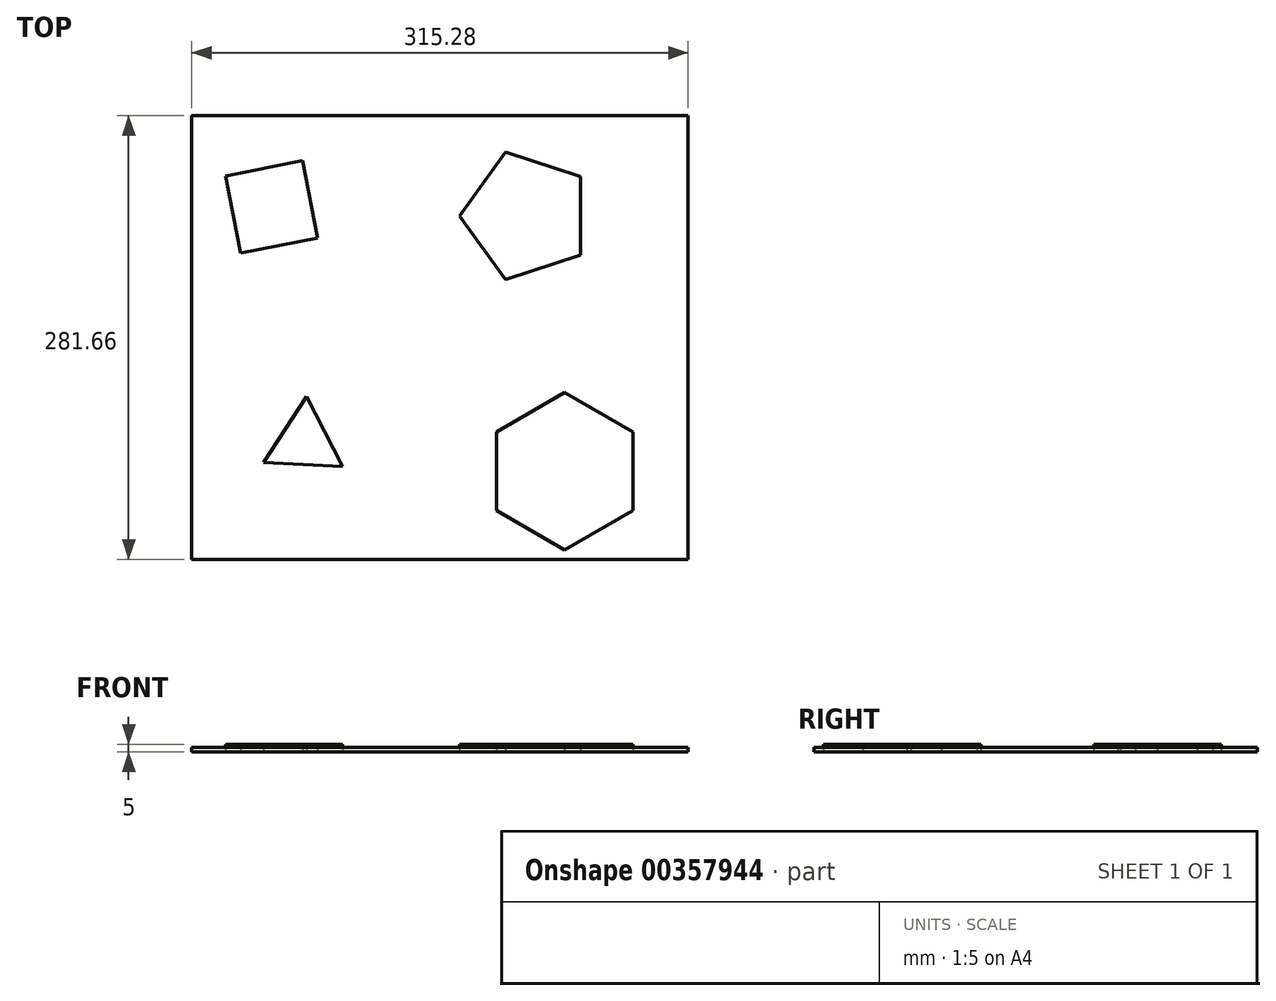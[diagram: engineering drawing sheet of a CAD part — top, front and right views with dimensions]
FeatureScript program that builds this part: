
annotation { "Feature Type Name" : "Feature", "Feature Type Description" : "" }
export const myFeature = defineFeature(function(context is Context, id is Id, definition is map)
    precondition{}
    {
        {
            var Q0;
            Q0=qCreatedBy(makeId("Top.planeOp"),FACE);
            var sketch = newSketch(context, id + "F0", { "sketchPlane" : qUnion([Q0])});
            skLineSegment(sketch, "E0.bottom", {"start": v(157.64, 140.83) * mm, "end": v(-157.64, 140.83) * mm});
            skLineSegment(sketch, "E0.top", {"start": v(157.64, -140.83) * mm, "end": v(-157.64, -140.83) * mm});
            skLineSegment(sketch, "E0.left", {"start": v(157.64, 140.83) * mm, "end": v(157.64, -140.83) * mm});
            skLineSegment(sketch, "E0.right", {"start": v(-157.64, 140.83) * mm, "end": v(-157.64, -140.83) * mm});
            skPoint(sketch, "E0.middle", {"position": v(0, 0) * mm});
            skSolve(sketch);
        }
        {
            var Q0;
            Q0=makeQuery(id+"F0.imprint","IMPRINT",FACE,{"disambiguationData":[TD([[makeQuery(id+"F0.imprint","IMPRINT",EDGE,{"derivedFrom":sQuery(id+"F0.wireOp",EDGE,"E0.bottom")}),1.0]])]});
            extrude(context, id + "F1", {"entities" : qUnion([Q0]), "depth" : 3 * mm});
        }
        {
            var Q0;
            Q0=qCreatedBy(makeId("Top.planeOp"),FACE);
            var sketch = newSketch(context, id + "F2", { "sketchPlane" : qUnion([Q0])});
            skCircle(sketch, "E1.cCircle", {"center": v(-86.17, -66.22) * mm, "radius": 14.43 * mm, "construction": true});
            skLineSegment(sketch, "E1.0", {"start": v(-84.62, -37.4) * mm, "end": v(-61.98, -81.97) * mm});
            skLineSegment(sketch, "E1.1", {"start": v(-61.98, -81.97) * mm, "end": v(-111.9, -79.3) * mm});
            skLineSegment(sketch, "E1.2", {"start": v(-111.9, -79.3) * mm, "end": v(-84.62, -37.4) * mm});
            skPoint(sketch, "E1.0.midPoint", {"position": v(-73.3, -59.68) * mm});
            skCircle(sketch, "E2.cCircle", {"center": v(-106.97, 82.94) * mm, "radius": 25 * mm, "construction": true});
            skLineSegment(sketch, "E2.0", {"start": v(-87.26, 112.3) * mm, "end": v(-77.61, 63.23) * mm});
            skLineSegment(sketch, "E2.1", {"start": v(-77.61, 63.23) * mm, "end": v(-126.67, 53.58) * mm});
            skLineSegment(sketch, "E2.2", {"start": v(-126.67, 53.58) * mm, "end": v(-136.32, 102.64) * mm});
            skLineSegment(sketch, "E2.3", {"start": v(-136.32, 102.64) * mm, "end": v(-87.26, 112.3) * mm});
            skPoint(sketch, "E2.0.midPoint", {"position": v(-82.44, 87.76) * mm});
            skCircle(sketch, "E3.cCircle", {"center": v(54.84, 77.23) * mm, "radius": 34.4 * mm, "construction": true});
            skLineSegment(sketch, "E3.0", {"start": v(89.25, 102.23) * mm, "end": v(89.25, 52.23) * mm});
            skLineSegment(sketch, "E3.1", {"start": v(89.25, 52.23) * mm, "end": v(41.7, 36.78) * mm});
            skLineSegment(sketch, "E3.2", {"start": v(41.7, 36.78) * mm, "end": v(12.3, 77.23) * mm});
            skLineSegment(sketch, "E3.3", {"start": v(12.3, 77.23) * mm, "end": v(41.7, 117.68) * mm});
            skLineSegment(sketch, "E3.4", {"start": v(41.7, 117.68) * mm, "end": v(89.25, 102.23) * mm});
            skPoint(sketch, "E3.0.midPoint", {"position": v(89.25, 77.23) * mm});
            skCircle(sketch, "E4.cCircle", {"center": v(79.22, -85) * mm, "radius": 43.3 * mm, "construction": true});
            skLineSegment(sketch, "E4.0", {"start": v(122.52, -60) * mm, "end": v(122.52, -110) * mm});
            skLineSegment(sketch, "E4.1", {"start": v(122.52, -110) * mm, "end": v(79.22, -135) * mm});
            skLineSegment(sketch, "E4.2", {"start": v(79.22, -135) * mm, "end": v(35.92, -110) * mm});
            skLineSegment(sketch, "E4.3", {"start": v(35.92, -110) * mm, "end": v(35.92, -60) * mm});
            skLineSegment(sketch, "E4.4", {"start": v(35.92, -60) * mm, "end": v(79.22, -35) * mm});
            skLineSegment(sketch, "E4.5", {"start": v(79.22, -35) * mm, "end": v(122.52, -60) * mm});
            skPoint(sketch, "E4.0.midPoint", {"position": v(122.52, -85) * mm});
            skSolve(sketch);
        }
        {
            assignVariable(context, id + "F3", {"name" : "tile_thickness", "anyValue" : 5});
        }
        {
            var Q0;
            Q0=makeQuery(id+"F2.imprint","IMPRINT",FACE,{"disambiguationData":[TD([[makeQuery(id+"F2.imprint","IMPRINT",EDGE,{"derivedFrom":sQuery(id+"F2.wireOp",EDGE,"E2.0")}),-1.0]])]});
            var Q1;
            Q1=makeQuery(id+"F2.imprint","IMPRINT",FACE,{"disambiguationData":[TD([[makeQuery(id+"F2.imprint","IMPRINT",EDGE,{"derivedFrom":sQuery(id+"F2.wireOp",EDGE,"E3.0")}),-1.0]])]});
            var Q2;
            Q2=makeQuery(id+"F2.imprint","IMPRINT",FACE,{"disambiguationData":[TD([[makeQuery(id+"F2.imprint","IMPRINT",EDGE,{"derivedFrom":sQuery(id+"F2.wireOp",EDGE,"E1.0")}),-1.0]])]});
            var Q3;
            Q3=makeQuery(id+"F2.imprint","IMPRINT",FACE,{"disambiguationData":[TD([[makeQuery(id+"F2.imprint","IMPRINT",EDGE,{"derivedFrom":sQuery(id+"F2.wireOp",EDGE,"E4.0")}),-1.0]])]});
            extrude(context, id + "F4", {"entities" : qUnion([Q0, Q1, Q2, Q3]), "depth" : (getVariable(context, 'tile_thickness')) * mm});
        }
    });
